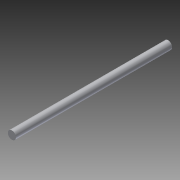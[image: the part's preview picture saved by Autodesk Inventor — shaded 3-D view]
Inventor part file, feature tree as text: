
AUTODESK INVENTOR PART (.ipt)
format: ipt  version: 2014 (Build 180170000, 170)  size: 78,336 bytes
history: native  units: in
note: dims shown in document units (in); Inventor stores cm internally (conversion verified against a paired STEP export)
features: extrude x1, sketch x1
ambient origin geometry x8: Origin, YZ Plane, XZ Plane, XY Plane, X Axis, Y Axis, Z Axis, Center Point
bodies: Solid1 (feature_tree)
feature tree (2):
  extrude  "Extrusion1"  Depth=12.0in TaperAngle=0.0deg
  sketch  "Sketch1"  dims[d0=0.625in d1=12.0in d2=0.0in]
